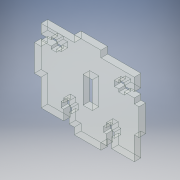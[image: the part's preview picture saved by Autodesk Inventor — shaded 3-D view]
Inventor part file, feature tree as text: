
AUTODESK INVENTOR PART (.ipt)
format: ipt  version: 2019 (Build 230136000, 136)  size: 314,880 bytes
history: native  units: mm
features: extrude x4, sketch x4, projected_geometry x2
ambient origin geometry x8: Origin, YZ Plane, XZ Plane, XY Plane, X Axis, Y Axis, Z Axis, Center Point
bodies: Solid1 (feature_tree)
feature tree (10):
  extrude  "Extrusion1"  Depth=55.0mm
  extrude  "Extrusion2"  Depth=20.0mm
  extrude  "Extrusion3"  Depth=25.0mm
  extrude  "Extrusion4"  Depth=20.0mm
  sketch  "Sketch1"  dims[d0=70.0mm d1=55.0mm]
  sketch  "Sketch2"  dims[d2=5.0mm d3=0.0mm d4=20.0mm]
  projected_geometry  "Projected Loop1"
  sketch  "Sketch3"  dims[d5=5.0mm d6=25.0mm]
  sketch  "Sketch4"  dims[d7=5.0mm d8=20.0mm d9=20.0mm d10=20.0mm d11=5.0mm d12=25.0mm d13=4.0mm d14=15.0mm d15=8.0mm d16=4.0mm d22=4.0mm d23=15.0mm d24=8.0mm d25=4.0mm d26=4.0mm d28=4.0mm d29=15.0mm d30=8.0mm d31=4.0mm d32=4.0mm d33=15.0mm d34=8.0mm d35=4.0mm d36=8.0mm d37=4.0mm d38=3.5mm d39=20.0mm d40=17.5mm d41=4.0mm d42=5.0mm d43=0.0mm d44=20.0mm d45=5.0mm d46=25.0mm d47=5.0mm d48=20.0mm d49=20.0mm d50=25.0mm d51=5.0mm d52=20.0mm d53=4.0mm d54=15.0mm d55=8.0mm d56=4.0mm d57=4.0mm d58=15.0mm d59=8.0mm d60=4.0mm d61=4.0mm d62=4.0mm d63=15.0mm d64=8.0mm d65=4.0mm d66=4.0mm d67=15.0mm d68=8.0mm d69=4.0mm d70=8.0mm d71=4.0mm d72=5.0mm d73=20.0mm d74=17.5mm d75=4.0mm d76=5.0mm d77=0.0mm d80=7.0mm d81=20.0mm d82=10.0mm d83=0.0mm]
  projected_geometry  "Projected Loop2"
